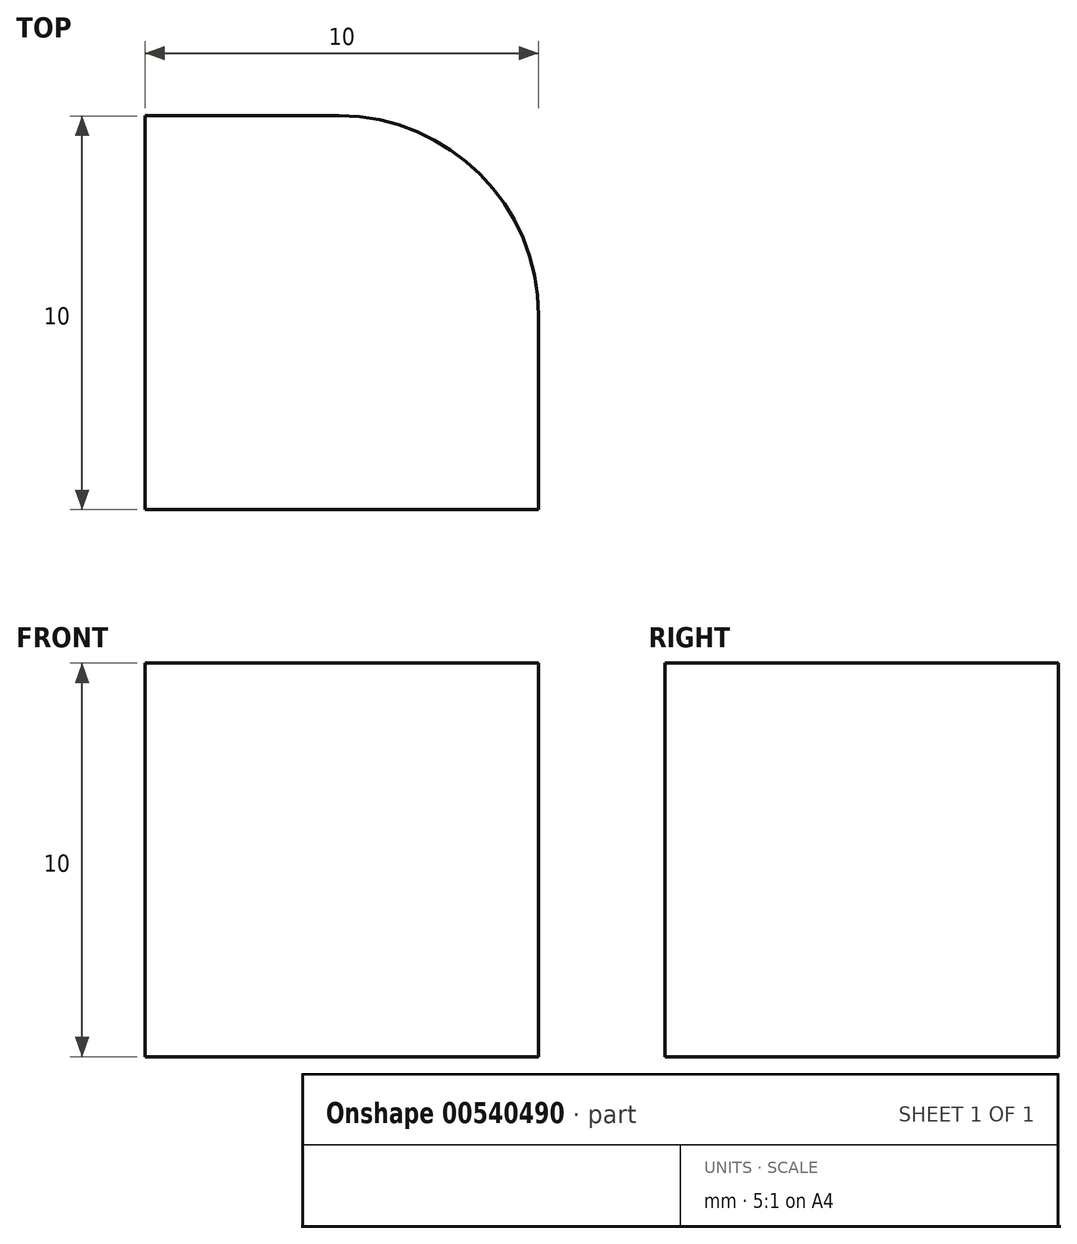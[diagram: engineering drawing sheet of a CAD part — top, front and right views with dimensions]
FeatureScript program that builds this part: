
annotation { "Feature Type Name" : "Feature", "Feature Type Description" : "" }
export const myFeature = defineFeature(function(context is Context, id is Id, definition is map)
    precondition{}
    {
        {
            var Q0;
            Q0=qCreatedBy(makeId("Top.planeOp"),FACE);
            var sketch = newSketch(context, id + "F0", { "sketchPlane" : qUnion([Q0])});
            skLineSegment(sketch, "E0.bottom", {"start": v(-13.86, 13.38) * mm, "end": v(-8.93, 13.38) * mm});
            skLineSegment(sketch, "E0.top", {"start": v(-13.86, 3.38) * mm, "end": v(-3.86, 3.38) * mm});
            skLineSegment(sketch, "E0.left", {"start": v(-13.86, 13.38) * mm, "end": v(-13.86, 3.38) * mm});
            skLineSegment(sketch, "E0.right", {"start": v(-3.86, 8.31) * mm, "end": v(-3.86, 3.38) * mm});
            skPoint(sketch, "E1.visualSharp", {"position": v(-3.86, 13.38) * mm});
            skArc(sketch, "E1.filletArc", {"start": v(-3.86, 8.31) * mm, "mid": v(-5.34, 11.9) * mm, "end": v(-8.93, 13.38) * mm});
            skSolve(sketch);
        }
        {
            var Q0;
            Q0=makeQuery(id+"F0.imprint","IMPRINT",FACE,{"disambiguationData":[TD([[makeQuery(id+"F0.imprint","IMPRINT",EDGE,{"derivedFrom":sQuery(id+"F0.wireOp",EDGE,"E0.bottom")}),-1.0]])]});
            extrude(context, id + "F1", {"entities" : qUnion([Q0]), "depth" : 10 * mm, "offsetDistance" : 25 * mm});
        }
    });
